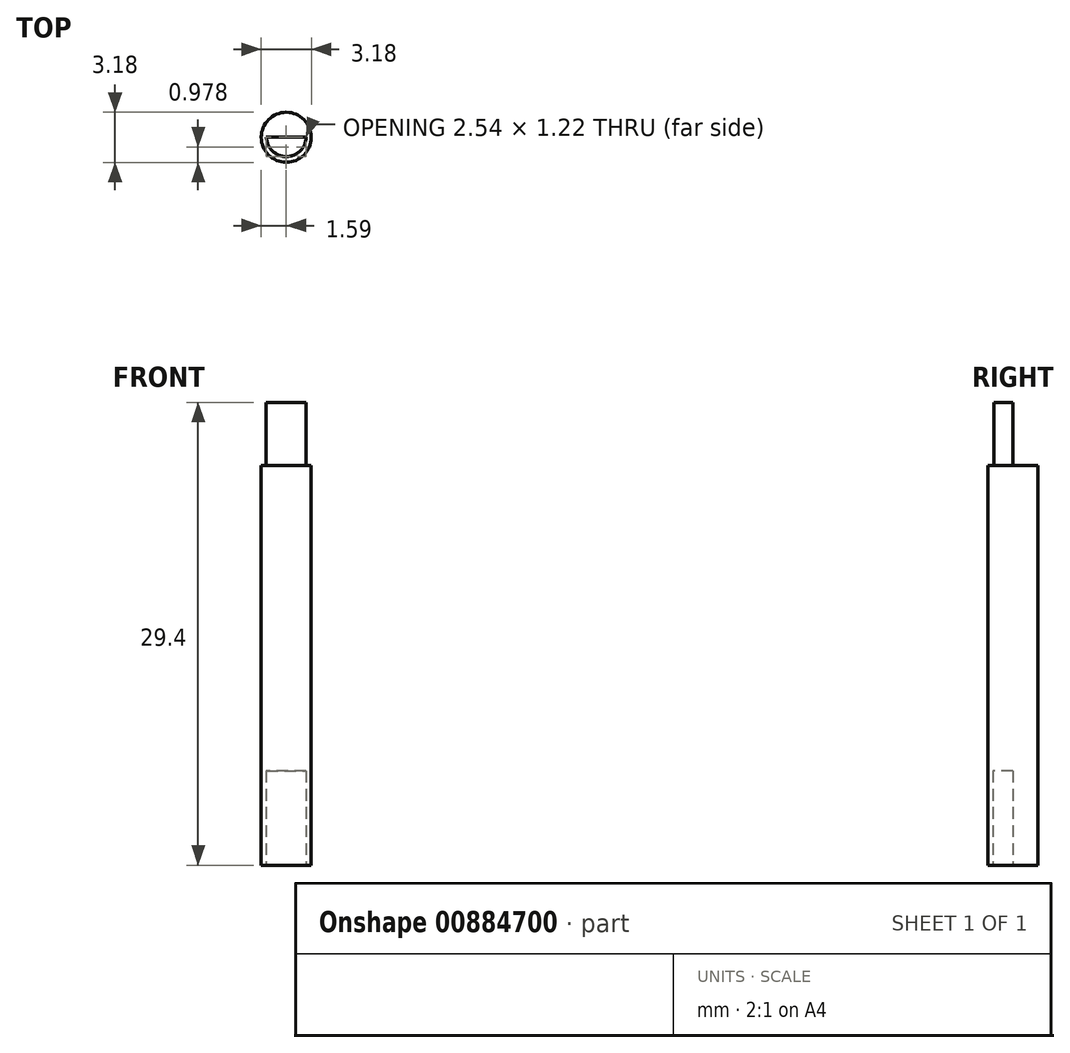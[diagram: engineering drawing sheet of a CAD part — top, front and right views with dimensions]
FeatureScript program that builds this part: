
annotation { "Feature Type Name" : "Feature", "Feature Type Description" : "" }
export const myFeature = defineFeature(function(context is Context, id is Id, definition is map)
    precondition{}
    {
        {
            var Q0;
            Q0=qCreatedBy(makeId("Top.planeOp"),FACE);
            var sketch = newSketch(context, id + "F0", { "sketchPlane" : qUnion([Q0])});
            skCircle(sketch, "E0", {"center": v(0, 0) * mm, "radius": 1.59 * mm});
            skSolve(sketch);
        }
        {
            var Q0;
            Q0 = qSketchRegion(id + "F0", true);
            extrude(context, id + "F1", {"entities" : qUnion([Q0]), "depth" : 25.4 * mm, "offsetDistance" : 25.4 * mm});
        }
        {
            var Q0;
            Q0=makeQuery(id+"F1.opExtrude","CAP_FACE",FACE,{"disambiguationData":[OSD([sQuery(id+"F0.wireOp",EDGE,"E0")])],"isStart":false});
            var sketch = newSketch(context, id + "F2", { "sketchPlane" : qUnion([Q0])});
            skLineSegment(sketch, "E1", {"start": v(1.27, 0) * mm, "end": v(-1.27, 0) * mm});
            skArc(sketch, "E2", {"start": v(-1.27, 0) * mm, "mid": v(0, -1.22) * mm, "end": v(1.27, 0) * mm});
            skSolve(sketch);
        }
        {
            var Q0;
            Q0 = qSketchRegion(id + "F2", true);
            extrude(context, id + "F3", {"entities" : qUnion([Q0]), "operationType" : NewBodyOperationType.ADD, "depth" : 4 * mm, "offsetDistance" : 25.4 * mm});
        }
        {
            var Q0;
            Q0=makeQuery(id+"F1.opExtrude","CAP_FACE",FACE,{"disambiguationData":[OSD([sQuery(id+"F0.wireOp",EDGE,"E0")])],"isStart":true});
            var sketch = newSketch(context, id + "F4", { "sketchPlane" : qUnion([Q0])});
            skLineSegment(sketch, "E3", {"start": v(-1.27, 0) * mm, "end": v(1.27, 0) * mm});
            skArc(sketch, "E4", {"start": v(1.27, 0) * mm, "mid": v(0, 1.27) * mm, "end": v(-1.27, 0) * mm});
            skSolve(sketch);
        }
        {
            var Q0;
            Q0=makeQuery(id+"F4.imprint","IMPRINT",FACE,{"disambiguationData":[TD([[makeQuery(id+"F4.imprint","IMPRINT",EDGE,{"derivedFrom":sQuery(id+"F4.wireOp",EDGE,"E3")}),1.0]])]});
            extrude(context, id + "F5", {"entities" : qUnion([Q0]), "operationType" : NewBodyOperationType.REMOVE, "oppositeDirection" : true, "depth" : 6 * mm, "offsetDistance" : 25.4 * mm});
        }
    });
